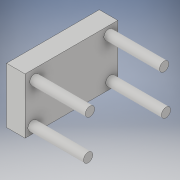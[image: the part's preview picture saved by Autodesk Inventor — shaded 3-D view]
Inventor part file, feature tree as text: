
AUTODESK INVENTOR PART (.ipt)
format: ipt  version: 2019 (Build 230136000, 136)  size: 128,512 bytes
history: native  units: in
note: dims shown in document units (in); Inventor stores cm internally (conversion verified against a paired STEP export)
features: extrude x2, sketch x2, other x1, plane x1, projected_geometry x1
ambient origin geometry x8: Origin, YZ Plane, XZ Plane, XY Plane, X Axis, Y Axis, Z Axis, Center Point
bodies: Solid1 (feature_tree)
feature tree (7):
  other  "Table"
  plane  "Work Plane1"
  extrude  "Extrusion1"  Depth=5.0in
  extrude  "Extrusion2"  Depth=1.0in TaperAngle=0.0deg
  sketch  "Sketch1"  dims[d0=0.125in d1=5.0in]
  sketch  "Sketch2"  dims[d2=3.0in d3=1.0in d4=0.0in d5=0.5in d6=0.4in d7=0.4in d8=0.4in d9=0.5in d10=0.5in d11=0.5in d12=0.5in d13=0.5in d14=0.5in d15=0.4in d16=0.4in d17=3.0in d18=0.0in]
  projected_geometry  "Projected Loop1"
